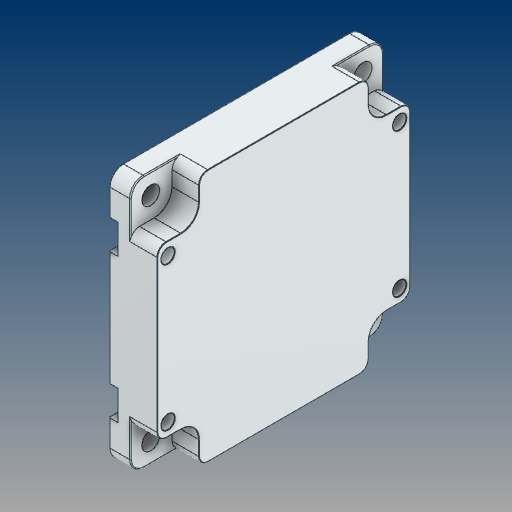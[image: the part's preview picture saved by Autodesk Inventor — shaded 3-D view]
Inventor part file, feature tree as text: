
AUTODESK INVENTOR PART (.ipt)
format: ipt  version: 2021 (Build 250183000, 183)  size: 246,784 bytes
history: native  units: mm
features: chamfer x1
ambient origin geometry x8: Origin, YZ Plane, XZ Plane, XY Plane, X Axis, Y Axis, Z Axis, Center Point
bodies: Solid1 (feature_tree)
feature tree (1):
  chamfer  "Chamfer3"  [1 undecoded]
note: 1 required parameter value undecoded (feature->parameter linkage not recoverable at this tier; creation-order binding heuristic only, values carry confidence <= 0.55)
